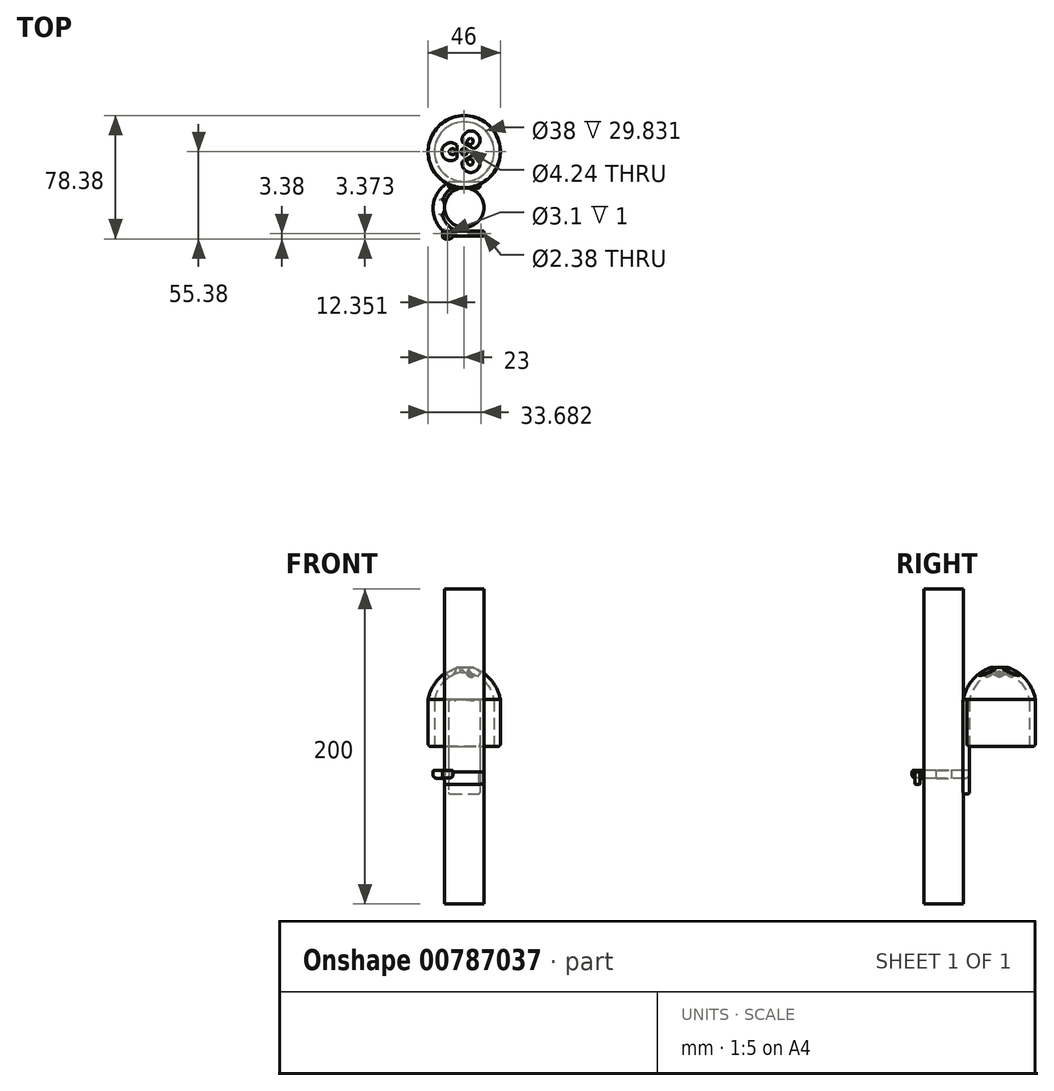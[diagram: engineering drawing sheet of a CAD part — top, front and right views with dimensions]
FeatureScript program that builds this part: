
annotation { "Feature Type Name" : "Feature", "Feature Type Description" : "" }
export const myFeature = defineFeature(function(context is Context, id is Id, definition is map)
    precondition{}
    {
        {
            var Q0;
            Q0=qCreatedBy(makeId("Top.planeOp"),FACE);
            var sketch = newSketch(context, id + "F0", { "sketchPlane" : qUnion([Q0])});
            skCircle(sketch, "E0", {"center": v(0, 0) * mm, "radius": 23 * mm});
            skSolve(sketch);
        }
        {
            var Q0;
            Q0 = qSketchRegion(id + "F0", true);
            extrude(context, id + "F1", {"entities" : qUnion([Q0]), "depth" : 30 * mm, "offsetDistance" : 25 * mm});
        }
        {
            var Q0;
            Q0=qCreatedBy(makeId("Top.planeOp"),FACE);
            var sketch = newSketch(context, id + "F2", { "sketchPlane" : qUnion([Q0])});
            skCircle(sketch, "E1", {"center": v(0, 0) * mm, "radius": 19 * mm});
            skSolve(sketch);
        }
        {
            var Q0;
            Q0 = qSketchRegion(id + "F2", true);
            extrude(context, id + "F3", {"entities" : qUnion([Q0]), "operationType" : NewBodyOperationType.REMOVE, "depth" : 30 * mm, "offsetDistance" : 25 * mm});
        }
        {
            var Q0;
            Q0=qCreatedBy(makeId("Front.planeOp"),FACE);
            cPlane(context, id + "F4", {"entities" : qUnion([Q0]), "cplaneType" : CPlaneType.OFFSET, "offset" : 21 * mm, "width" : 150 * mm, "height" : 150 * mm});
        }
        {
            var Q0;
            Q0=qCreatedBy(id+"F4.planeOp",FACE);
            var sketch = newSketch(context, id + "F5", { "sketchPlane" : qUnion([Q0])});
            skLineSegment(sketch, "E2.bottom", {"start": v(-10, 30) * mm, "end": v(10, 30) * mm});
            skLineSegment(sketch, "E2.top", {"start": v(-10, -30) * mm, "end": v(10, -30) * mm});
            skLineSegment(sketch, "E2.left", {"start": v(-10, 30) * mm, "end": v(-10, -30) * mm});
            skLineSegment(sketch, "E2.right", {"start": v(10, 30) * mm, "end": v(10, -30) * mm});
            skPoint(sketch, "E2.middle", {"position": v(0, 0) * mm});
            skSolve(sketch);
        }
        {
            var Q0;
            Q0 = qSketchRegion(id + "F5", true);
            extrude(context, id + "F6", {"entities" : qUnion([Q0]), "operationType" : NewBodyOperationType.ADD, "endBound" : BoundingType.SYMMETRIC, "depth" : 4 * mm, "offsetDistance" : 25 * mm});
        }
        {
            var Q0;
            Q0=qCreatedBy(makeId("Right.planeOp"),FACE);
            var sketch = newSketch(context, id + "F7", { "sketchPlane" : qUnion([Q0])});
            skArc(sketch, "E3", {"start": v(22.91, 29.83) * mm, "mid": v(15.03, 44.46) * mm, "end": v(0, 51.56) * mm});
            skLineSegment(sketch, "E4", {"start": v(22.91, 29.83) * mm, "end": v(18.91, 29.83) * mm});
            skLineSegment(sketch, "E5", {"start": v(0, 51.56) * mm, "end": v(0, 47.56) * mm});
            skArc(sketch, "E6", {"start": v(18.91, 29.83) * mm, "mid": v(12.4, 41.83) * mm, "end": v(0, 47.56) * mm});
            skSolve(sketch);
        }
        {
            var Q0;
            Q0=makeQuery(id+"F7.imprint","IMPRINT",FACE,{"disambiguationData":[TD([[makeQuery(id+"F7.imprint","IMPRINT",EDGE,{"derivedFrom":sQuery(id+"F7.wireOp",EDGE,"E3")}),1.0]])]});
            var Q1;
            Q1=sQuery(id+"F7.wireOp",EDGE,"E5");
            revolve(context, id + "F8", {"operationType" : NewBodyOperationType.ADD, "surfaceOperationType" : NewSurfaceOperationType.NEW, "entities" : qUnion([Q0]), "axis" : qUnion([Q1]), "revolveType" : RevolveType.FULL});
        }
        {
            var Q0;
            Q0=qCreatedBy(makeId("Top.planeOp"),FACE);
            var sketch = newSketch(context, id + "F9", { "sketchPlane" : qUnion([Q0])});
            skCircle(sketch, "E7", {"center": v(-7.43, 0) * mm, "radius": 1.87 * mm});
            skCircle(sketch, "E8.1.0", {"center": v(3.71, 6.43) * mm, "radius": 1.87 * mm});
            skCircle(sketch, "E8.2.0", {"center": v(3.71, -6.43) * mm, "radius": 1.87 * mm});
            skPoint(sketch, "E8.center", {"position": v(0, 0) * mm});
            skLineSegment(sketch, "E8.anchor1", {"start": v(0, 0) * mm, "end": v(-7.43, 0) * mm, "construction": true});
            skLineSegment(sketch, "E8.anchor2", {"start": v(0, 0) * mm, "end": v(3.71, -6.43) * mm, "construction": true});
            skCircle(sketch, "E9", {"center": v(0, 0) * mm, "radius": 2.12 * mm});
            skSolve(sketch);
        }
        {
            var Q0;
            Q0=makeQuery(id+"F9.imprint","IMPRINT",FACE,{"disambiguationData":[TD([[makeQuery(id+"F9.imprint","IMPRINT",EDGE,{"derivedFrom":sQuery(id+"F9.wireOp",EDGE,"E9")}),1.0]])]});
            var Q1;
            Q1=makeQuery(id+"F9.imprint","IMPRINT",FACE,{"disambiguationData":[TD([[makeQuery(id+"F9.imprint","IMPRINT",EDGE,{"derivedFrom":sQuery(id+"F9.wireOp",EDGE,"E7")}),1.0]])]});
            var Q2;
            Q2=makeQuery(id+"F9.imprint","IMPRINT",FACE,{"disambiguationData":[TD([[makeQuery(id+"F9.imprint","IMPRINT",EDGE,{"derivedFrom":sQuery(id+"F9.wireOp",EDGE,"E8.1.0")}),1.0]])]});
            var Q3;
            Q3=makeQuery(id+"F9.imprint","IMPRINT",FACE,{"disambiguationData":[TD([[makeQuery(id+"F9.imprint","IMPRINT",EDGE,{"derivedFrom":sQuery(id+"F9.wireOp",EDGE,"E8.2.0")}),1.0]])]});
            extrude(context, id + "F10", {"entities" : qUnion([Q0, Q1, Q2, Q3]), "operationType" : NewBodyOperationType.REMOVE, "endBound" : BoundingType.THROUGH_ALL, "depth" : 25 * mm, "offsetDistance" : 25 * mm});
        }
        {
            var Q0;
            Q0=qCreatedBy(makeId("Front.planeOp"),FACE);
            var sketch = newSketch(context, id + "F11", { "sketchPlane" : qUnion([Q0])});
            skPoint(sketch, "E10", {"position": v(-4.85, -20.06) * mm});
            skSolve(sketch);
        }
        {
            var Q0;
            Q0=sQuery(id+"F11.wireOp",VERTEX,"E10");
            var Q1;
            Q1=qCreatedBy(makeId("Top.planeOp"),FACE);
            cPlane(context, id + "F12", {"entities" : qUnion([Q0, Q1]), "cplaneType" : CPlaneType.PLANE_POINT, "offset" : 25 * mm, "width" : 150 * mm, "height" : 150 * mm});
        }
        {
            var Q0;
            Q0=qCreatedBy(id+"F12.planeOp",FACE);
            var sketch = newSketch(context, id + "F13", { "sketchPlane" : qUnion([Q0])});
            skPoint(sketch, "E11.second.point", {"position": v(-3.53, -23.55) * mm});
            skArc(sketch, "E12", {"start": v(-7.93, -23) * mm, "mid": v(-14.65, -36.3) * mm, "end": v(-7.21, -49.21) * mm});
            skArc(sketch, "E13", {"start": v(-9.46, -19.23) * mm, "mid": v(-19.78, -36.18) * mm, "end": v(-9.46, -53.12) * mm});
            skLineSegment(sketch, "E14", {"start": v(-7.93, -23) * mm, "end": v(-9.46, -19.23) * mm});
            skArc(sketch, "E15.MirrorCS", {"start": v(9.46, -19.23) * mm, "mid": v(19.78, -36.18) * mm, "end": v(9.46, -53.12) * mm});
            skLineSegment(sketch, "E16.MirrorCS", {"start": v(7.93, -23) * mm, "end": v(9.46, -19.23) * mm});
            skArc(sketch, "E17.MirrorCS", {"start": v(7.93, -23) * mm, "mid": v(14.65, -36.3) * mm, "end": v(7.21, -49.21) * mm});
            skLineSegment(sketch, "E18.top", {"start": v(-9.21, -55.38) * mm, "end": v(-11.96, -55.38) * mm});
            skLineSegment(sketch, "E18.left", {"start": v(-7.21, -49.21) * mm, "end": v(-7.21, -53.38) * mm});
            skLineSegment(sketch, "E18.right", {"start": v(-13.96, -49.74) * mm, "end": v(-13.96, -53.38) * mm});
            skLineSegment(sketch, "E19.MirrorCS", {"start": v(7.21, -49.21) * mm, "end": v(7.21, -53.38) * mm});
            skLineSegment(sketch, "E20.MirrorCS", {"start": v(9.21, -55.38) * mm, "end": v(11.96, -55.38) * mm});
            skLineSegment(sketch, "E21.MirrorCS", {"start": v(13.96, -49.74) * mm, "end": v(13.96, -53.38) * mm});
            skPoint(sketch, "E22.visualSharp", {"position": v(13.96, -55.38) * mm});
            skArc(sketch, "E22.filletArc", {"start": v(11.96, -55.38) * mm, "mid": v(13.37, -54.8) * mm, "end": v(13.96, -53.38) * mm});
            skPoint(sketch, "E23.visualSharp", {"position": v(7.21, -55.38) * mm});
            skArc(sketch, "E23.filletArc", {"start": v(7.21, -53.38) * mm, "mid": v(7.8, -54.8) * mm, "end": v(9.21, -55.38) * mm});
            skPoint(sketch, "E24.visualSharp", {"position": v(-7.21, -55.38) * mm});
            skArc(sketch, "E24.filletArc", {"start": v(-9.21, -55.38) * mm, "mid": v(-7.8, -54.8) * mm, "end": v(-7.21, -53.38) * mm});
            skPoint(sketch, "E25.visualSharp", {"position": v(-13.96, -55.38) * mm});
            skArc(sketch, "E25.filletArc", {"start": v(-13.96, -53.38) * mm, "mid": v(-13.37, -54.8) * mm, "end": v(-11.96, -55.38) * mm});
            skPoint(sketch, "E26", {"position": v(-11.02, -52.23) * mm});
            skPoint(sketch, "E27.MirrorP", {"position": v(11.02, -52.23) * mm});
            skArc(sketch, "E28", {"start": v(-14.02, -40.31) * mm, "mid": v(-12.35, -35.41) * mm, "end": v(-13.68, -30.4) * mm});
            skArc(sketch, "E29.MirrorCS", {"start": v(14.02, -40.31) * mm, "mid": v(12.35, -35.41) * mm, "end": v(13.68, -30.4) * mm});
            skSolve(sketch);
        }
        {
            var Q0;
            Q0=makeQuery(id+"F13.imprint","IMPRINT",FACE,{"disambiguationData":[TD([[makeQuery(id+"F13.imprint","IMPRINT",EDGE,{"derivedFrom":sQuery(id+"F13.wireOp",EDGE,"E12")}),-1.0]])]});
            var Q1;
            Q1=makeQuery(id+"F13.imprint","IMPRINT",FACE,{"disambiguationData":[TD([[makeQuery(id+"F13.imprint","IMPRINT",EDGE,{"derivedFrom":sQuery(id+"F13.wireOp",EDGE,"E15.MirrorCS")}),-1.0]])]});
            var Q2;
            {var subQ0=sQuery(id+"F13.wireOp",EDGE,"E28");Q2=makeQuery(id+"F13.imprint","IMPRINT",FACE,{"disambiguationData":[TD([[makeQuery(id+"F13.imprint","IMPRINT",EDGE,{"derivedFrom":subQ0}),1.0]])]});}
            var Q3;
            {var subQ0=sQuery(id+"F13.wireOp",EDGE,"E29.MirrorCS");Q3=makeQuery(id+"F13.imprint","IMPRINT",FACE,{"disambiguationData":[TD([[makeQuery(id+"F13.imprint","IMPRINT",EDGE,{"derivedFrom":subQ0}),-1.0]])]});}
            extrude(context, id + "F14", {"entities" : qUnion([Q0, Q1, Q2, Q3]), "operationType" : NewBodyOperationType.ADD, "depth" : 5 * mm, "offsetDistance" : 25 * mm});
        }
        {
            var Q0;
            Q0=makeQuery(id+"F3.boolean.opBoolean","COPY",EDGE,{"derivedFrom":makeQuery(id+"F3.opExtrude","CAP_EDGE",EDGE,{"disambiguationData":[OSD([sQuery(id+"F2.wireOp",EDGE,"E1")])],"isStart":true})});
            var Q1;
            {var subQ0=sQuery(id+"F0.wireOp",EDGE,"E0");Q1=makeQuery(id+"F6.boolean.opBoolean","SPLIT",EDGE,{"disambiguationData":[TD([makeQuery(id+"F6.opExtrude","SWEPT_FACE",FACE,{"disambiguationData":[OSD([sQuery(id+"F5.wireOp",EDGE,"E2.left")])]})])],"derivedFrom":makeQuery(id+"F1.opExtrude","CAP_EDGE",EDGE,{"disambiguationData":[OSD([subQ0])],"isStart":true})});}
            fillet(context, id + "F15", {"entities" : qUnion([Q0, Q1]), "radius" : 2 * mm, "tangentPropagation" : true, "allowEdgeOverflow" : false});
        }
        {
            var Q0;
            Q0=qCreatedBy(makeId("Top.planeOp"),FACE);
            var sketch = newSketch(context, id + "F16", { "sketchPlane" : qUnion([Q0])});
            skCircle(sketch, "E30", {"center": v(0, -35.47) * mm, "radius": 12.5 * mm});
            skSolve(sketch);
        }
        {
            var Q0;
            Q0 = qSketchRegion(id + "F16", true);
            extrude(context, id + "F17", {"entities" : qUnion([Q0]), "endBound" : BoundingType.SYMMETRIC, "depth" : 200 * mm, "offsetDistance" : 25 * mm});
        }
        {
            var Q0;
            Q0=makeQuery(id+"F14.opExtrude","CAP_FACE",FACE,{"disambiguationData":[OSD([sQuery(id+"F13.wireOp",EDGE,"E12"),sQuery(id+"F13.wireOp",EDGE,"E13"),sQuery(id+"F13.wireOp",EDGE,"E14"),sQuery(id+"F13.wireOp",EDGE,"E18.top"),sQuery(id+"F13.wireOp",EDGE,"E18.left"),sQuery(id+"F13.wireOp",EDGE,"E18.right"),sQuery(id+"F13.wireOp",EDGE,"E24.filletArc"),sQuery(id+"F13.wireOp",EDGE,"E25.filletArc")])],"isStart":true});
            var sketch = newSketch(context, id + "F18", { "sketchPlane" : qUnion([Q0])});
            skCircle(sketch, "E31", {"center": v(-10.65, 52) * mm, "radius": 1.55 * mm});
            skCircle(sketch, "E32.MirrorC", {"center": v(10.65, 52) * mm, "radius": 1.55 * mm});
            skSolve(sketch);
        }
        {
            var Q0;
            Q0=makeQuery(id+"F18.imprint","IMPRINT",FACE,{"disambiguationData":[TD([[makeQuery(id+"F18.imprint","IMPRINT",EDGE,{"derivedFrom":sQuery(id+"F18.wireOp",EDGE,"E31")}),1.0]])]});
            var Q1;
            Q1=makeQuery(id+"F18.imprint","IMPRINT",FACE,{"disambiguationData":[TD([[makeQuery(id+"F18.imprint","IMPRINT",EDGE,{"derivedFrom":sQuery(id+"F18.wireOp",EDGE,"E32.MirrorC")}),-1.0]])]});
            extrude(context, id + "F19", {"entities" : qUnion([Q0, Q1]), "operationType" : NewBodyOperationType.REMOVE, "endBound" : BoundingType.THROUGH_ALL, "oppositeDirection" : true, "depth" : 25 * mm, "offsetDistance" : 25 * mm});
        }
        {
            var Q0;
            Q0=makeQuery(id+"F10.boolean.opBoolean","INTERSECT",EDGE,{"derivedFrom":[makeQuery(id+"F8.opRevolve","SWEPT_FACE",FACE,{"disambiguationData":[OSD([sQuery(id+"F7.wireOp",EDGE,"E3")])]}),makeQuery(id+"F10.opExtrude","SWEPT_FACE",FACE,{"disambiguationData":[OSD([sQuery(id+"F9.wireOp",EDGE,"E9")])]})]});
            var Q1;
            Q1=makeQuery(id+"F10.boolean.opBoolean","INTERSECT",EDGE,{"derivedFrom":[makeQuery(id+"F8.opRevolve","SWEPT_FACE",FACE,{"disambiguationData":[OSD([sQuery(id+"F7.wireOp",EDGE,"E3")])]}),makeQuery(id+"F10.opExtrude","SWEPT_FACE",FACE,{"disambiguationData":[OSD([sQuery(id+"F9.wireOp",EDGE,"E8.2.0")])]})]});
            var Q2;
            Q2=makeQuery(id+"F10.boolean.opBoolean","INTERSECT",EDGE,{"derivedFrom":[makeQuery(id+"F8.opRevolve","SWEPT_FACE",FACE,{"disambiguationData":[OSD([sQuery(id+"F7.wireOp",EDGE,"E3")])]}),makeQuery(id+"F10.opExtrude","SWEPT_FACE",FACE,{"disambiguationData":[OSD([sQuery(id+"F9.wireOp",EDGE,"E8.1.0")])]})]});
            var Q3;
            Q3=makeQuery(id+"F10.boolean.opBoolean","INTERSECT",EDGE,{"derivedFrom":[makeQuery(id+"F8.opRevolve","SWEPT_FACE",FACE,{"disambiguationData":[OSD([sQuery(id+"F7.wireOp",EDGE,"E3")])]}),makeQuery(id+"F10.opExtrude","SWEPT_FACE",FACE,{"disambiguationData":[OSD([sQuery(id+"F9.wireOp",EDGE,"E7")])]})]});
            fillet(context, id + "F20", {"entities" : qUnion([Q0, Q1, Q2, Q3]), "radius" : 3 * mm, "tangentPropagation" : true, "allowEdgeOverflow" : false});
        }
        {
            var Q0;
            {var subQ0=sQuery(id+"F13.wireOp",EDGE,"E15.MirrorCS");Q0=makeQuery(id+"F14.boolean.opBoolean","SPLIT",EDGE,{"disambiguationData":[TD([makeQuery(id+"F6.opExtrude","SWEPT_FACE",FACE,{"disambiguationData":[OSD([sQuery(id+"F5.wireOp",EDGE,"E2.right")])]})])],"derivedFrom":makeQuery(id+"F14.opExtrude","CAP_EDGE",EDGE,{"disambiguationData":[OSD([subQ0])],"isStart":true})});}
            var Q1;
            {var subQ0=sQuery(id+"F13.wireOp",EDGE,"E17.MirrorCS");Q1=makeQuery(id+"F14.opExtrude","CAP_EDGE",EDGE,{"disambiguationData":[OSD([subQ0]),TDD([makeQuery(id+"F13.imprint","IMPRINT",EDGE,{"disambiguationData":[TD([[makeQuery(id+"F13.imprint","INTERSECT",VERTEX,{"derivedFrom":[subQ0,sQuery(id+"F13.wireOp",EDGE,"E19.MirrorCS")]}),1.0]])],"derivedFrom":subQ0})])],"isStart":true});}
            var Q2;
            Q2=makeQuery(id+"F14.opExtrude","CAP_EDGE",EDGE,{"disambiguationData":[OSD([sQuery(id+"F13.wireOp",EDGE,"E29.MirrorCS")])],"isStart":true});
            var Q3;
            {var subQ0=sQuery(id+"F13.wireOp",EDGE,"E17.MirrorCS");Q3=makeQuery(id+"F14.opExtrude","CAP_EDGE",EDGE,{"disambiguationData":[OSD([subQ0]),TDD([makeQuery(id+"F13.imprint","IMPRINT",EDGE,{"disambiguationData":[TD([[makeQuery(id+"F13.imprint","INTERSECT",VERTEX,{"derivedFrom":[sQuery(id+"F13.wireOp",EDGE,"E16.MirrorCS"),subQ0]}),-1.0]])],"derivedFrom":subQ0})])],"isStart":true});}
            var Q4;
            Q4=makeQuery(id+"F14.opExtrude","CAP_EDGE",EDGE,{"disambiguationData":[OSD([sQuery(id+"F13.wireOp",EDGE,"E19.MirrorCS")])],"isStart":true});
            var Q5;
            Q5=makeQuery(id+"F14.opExtrude","CAP_EDGE",EDGE,{"disambiguationData":[OSD([sQuery(id+"F13.wireOp",EDGE,"E18.left")])],"isStart":true});
            var Q6;
            {var subQ1=sQuery(id+"F13.wireOp",EDGE,"E13");Q6=makeQuery(id+"F14.boolean.opBoolean","SPLIT",EDGE,{"disambiguationData":[TD([makeQuery(id+"F6.opExtrude","SWEPT_FACE",FACE,{"disambiguationData":[OSD([sQuery(id+"F5.wireOp",EDGE,"E2.left")])]})])],"derivedFrom":makeQuery(id+"F14.opExtrude","CAP_EDGE",EDGE,{"disambiguationData":[OSD([subQ1])],"isStart":true})});}
            var Q7;
            {var subQ0=sQuery(id+"F13.wireOp",EDGE,"E12");Q7=makeQuery(id+"F14.opExtrude","CAP_EDGE",EDGE,{"disambiguationData":[OSD([subQ0]),TDD([makeQuery(id+"F13.imprint","IMPRINT",EDGE,{"disambiguationData":[TD([[makeQuery(id+"F13.imprint","INTERSECT",VERTEX,{"derivedFrom":[subQ0,sQuery(id+"F13.wireOp",EDGE,"E18.left")]}),1.0]])],"derivedFrom":subQ0})])],"isStart":true});}
            var Q8;
            Q8=makeQuery(id+"F14.opExtrude","CAP_EDGE",EDGE,{"disambiguationData":[OSD([sQuery(id+"F13.wireOp",EDGE,"E28")])],"isStart":true});
            var Q9;
            {var subQ0=sQuery(id+"F13.wireOp",EDGE,"E12");Q9=makeQuery(id+"F14.opExtrude","CAP_EDGE",EDGE,{"disambiguationData":[OSD([subQ0]),TDD([makeQuery(id+"F13.imprint","IMPRINT",EDGE,{"disambiguationData":[TD([[makeQuery(id+"F13.imprint","INTERSECT",VERTEX,{"derivedFrom":[subQ0,sQuery(id+"F13.wireOp",EDGE,"E14")]}),-1.0]])],"derivedFrom":subQ0})])],"isStart":true});}
            fillet(context, id + "F21", {"entities" : qUnion([Q0, Q1, Q2, Q3, Q4, Q5, Q6, Q7, Q8, Q9]), "radius" : 2 * mm, "tangentPropagation" : true, "allowEdgeOverflow" : false});
        }
        {
            var Q0;
            Q0=makeQuery(id+"F6.opExtrude","CAP_EDGE",EDGE,{"disambiguationData":[OSD([sQuery(id+"F5.wireOp",EDGE,"E2.top")])],"isStart":true});
            var Q1;
            Q1=makeQuery(id+"F15.opFillet","BLEND_EDGE",EDGE,{"blendedFrom":[makeQuery(id+"F3.boolean.opBoolean","COPY",EDGE,{"derivedFrom":makeQuery(id+"F3.opExtrude","CAP_EDGE",EDGE,{"disambiguationData":[OSD([sQuery(id+"F2.wireOp",EDGE,"E1")])],"isStart":true})}),makeQuery(id+"F6.opExtrude","CAP_FACE",FACE,{"disambiguationData":[OSD([sQuery(id+"F5.wireOp",EDGE,"E2.bottom"),sQuery(id+"F5.wireOp",EDGE,"E2.top"),sQuery(id+"F5.wireOp",EDGE,"E2.left"),sQuery(id+"F5.wireOp",EDGE,"E2.right")])],"isStart":true})],"blendedInto":[makeQuery(id+"F6.opExtrude","CAP_FACE",FACE,{"disambiguationData":[OSD([sQuery(id+"F5.wireOp",EDGE,"E2.bottom"),sQuery(id+"F5.wireOp",EDGE,"E2.top"),sQuery(id+"F5.wireOp",EDGE,"E2.left"),sQuery(id+"F5.wireOp",EDGE,"E2.right")])],"isStart":true})]});
            var Q2;
            Q2=makeQuery(id+"F6.opExtrude","CAP_EDGE",EDGE,{"disambiguationData":[OSD([sQuery(id+"F5.wireOp",EDGE,"E2.top")])],"isStart":false});
            var Q3;
            {var subQ0=sQuery(id+"F5.wireOp",EDGE,"E2.left");var subQ1=sQuery(id+"F5.wireOp",EDGE,"E2.top");Q3=makeQuery(id+"F14.boolean.opBoolean","SPLIT",EDGE,{"disambiguationData":[TD([makeQuery(id+"F6.opExtrude","SWEPT_FACE",FACE,{"disambiguationData":[OSD([subQ1])]})])],"derivedFrom":makeQuery(id+"F6.opExtrude","CAP_EDGE",EDGE,{"disambiguationData":[OSD([subQ0])],"isStart":false})});}
            var Q4;
            {var subQ0=sQuery(id+"F5.wireOp",EDGE,"E2.right");var subQ1=sQuery(id+"F5.wireOp",EDGE,"E2.top");Q4=makeQuery(id+"F14.boolean.opBoolean","SPLIT",EDGE,{"disambiguationData":[TD([makeQuery(id+"F6.opExtrude","SWEPT_FACE",FACE,{"disambiguationData":[OSD([subQ1])]})])],"derivedFrom":makeQuery(id+"F6.opExtrude","CAP_EDGE",EDGE,{"disambiguationData":[OSD([subQ0])],"isStart":false})});}
            var Q5;
            {var subQ0=sQuery(id+"F5.wireOp",EDGE,"E2.right");Q5=makeQuery(id+"F14.boolean.opBoolean","SPLIT",EDGE,{"disambiguationData":[TD([makeQuery(id+"F1.opExtrude","CAP_FACE",FACE,{"disambiguationData":[OSD([sQuery(id+"F0.wireOp",EDGE,"E0")])],"isStart":false})])],"derivedFrom":makeQuery(id+"F6.opExtrude","CAP_EDGE",EDGE,{"disambiguationData":[OSD([subQ0])],"isStart":false})});}
            var Q6;
            {var subQ0=sQuery(id+"F5.wireOp",EDGE,"E2.left");Q6=makeQuery(id+"F14.boolean.opBoolean","SPLIT",EDGE,{"disambiguationData":[TD([makeQuery(id+"F1.opExtrude","CAP_FACE",FACE,{"disambiguationData":[OSD([sQuery(id+"F0.wireOp",EDGE,"E0")])],"isStart":false})])],"derivedFrom":makeQuery(id+"F6.opExtrude","CAP_EDGE",EDGE,{"disambiguationData":[OSD([subQ0])],"isStart":false})});}
            var Q7;
            {var subQ0=sQuery(id+"F5.wireOp",EDGE,"E2.bottom");var subQ2=sQuery(id+"F5.wireOp",EDGE,"E2.left");Q7=makeQuery(id+"F6.boolean.opBoolean","SPLIT",EDGE,{"disambiguationData":[TD([makeQuery(id+"F6.opExtrude","SWEPT_FACE",FACE,{"disambiguationData":[OSD([subQ2])]})])],"derivedFrom":makeQuery(id+"F6.opExtrude","CAP_EDGE",EDGE,{"disambiguationData":[OSD([subQ0])],"isStart":false})});}
            var Q8;
            {var subQ0=sQuery(id+"F5.wireOp",EDGE,"E2.bottom");var subQ2=sQuery(id+"F5.wireOp",EDGE,"E2.right");Q8=makeQuery(id+"F6.boolean.opBoolean","SPLIT",EDGE,{"disambiguationData":[TD([makeQuery(id+"F6.opExtrude","SWEPT_FACE",FACE,{"disambiguationData":[OSD([subQ2])]})])],"derivedFrom":makeQuery(id+"F6.opExtrude","CAP_EDGE",EDGE,{"disambiguationData":[OSD([subQ0])],"isStart":false})});}
            var Q9;
            Q9=makeQuery(id+"F6.opExtrude","CAP_EDGE",EDGE,{"disambiguationData":[OSD([sQuery(id+"F5.wireOp",EDGE,"E2.left")])],"isStart":true});
            var Q10;
            Q10=makeQuery(id+"F6.opExtrude","CAP_EDGE",EDGE,{"disambiguationData":[OSD([sQuery(id+"F5.wireOp",EDGE,"E2.right")])],"isStart":true});
            var Q11;
            Q11=makeQuery(id+"F6.opExtrude","SWEPT_EDGE",EDGE,{"disambiguationData":[OSD([sQuery(id+"F5.wireOp",EDGE,"E2.top"),sQuery(id+"F5.wireOp",EDGE,"E2.left")])]});
            var Q12;
            Q12=makeQuery(id+"F6.opExtrude","SWEPT_EDGE",EDGE,{"disambiguationData":[OSD([sQuery(id+"F5.wireOp",EDGE,"E2.top"),sQuery(id+"F5.wireOp",EDGE,"E2.right")])]});
            fillet(context, id + "F22", {"entities" : qUnion([Q0, Q1, Q2, Q3, Q4, Q5, Q6, Q7, Q8, Q9, Q10, Q11, Q12]), "radius" : 1 * mm, "tangentPropagation" : true, "allowEdgeOverflow" : false});
        }
        {
            var Q0;
            Q0=makeQuery(id+"F14.opExtrude","CAP_EDGE",EDGE,{"disambiguationData":[OSD([sQuery(id+"F13.wireOp",EDGE,"E29.MirrorCS")])],"isStart":false});
            var Q1;
            {var subQ0=sQuery(id+"F13.wireOp",EDGE,"E17.MirrorCS");Q1=makeQuery(id+"F14.opExtrude","CAP_EDGE",EDGE,{"disambiguationData":[OSD([subQ0]),TDD([makeQuery(id+"F13.imprint","IMPRINT",EDGE,{"disambiguationData":[TD([[makeQuery(id+"F13.imprint","INTERSECT",VERTEX,{"derivedFrom":[sQuery(id+"F13.wireOp",EDGE,"E16.MirrorCS"),subQ0]}),-1.0]])],"derivedFrom":subQ0})])],"isStart":false});}
            var Q2;
            {var subQ0=sQuery(id+"F13.wireOp",EDGE,"E17.MirrorCS");Q2=makeQuery(id+"F14.opExtrude","CAP_EDGE",EDGE,{"disambiguationData":[OSD([subQ0]),TDD([makeQuery(id+"F13.imprint","IMPRINT",EDGE,{"disambiguationData":[TD([[makeQuery(id+"F13.imprint","INTERSECT",VERTEX,{"derivedFrom":[subQ0,sQuery(id+"F13.wireOp",EDGE,"E19.MirrorCS")]}),1.0]])],"derivedFrom":subQ0})])],"isStart":false});}
            var Q3;
            Q3=makeQuery(id+"F14.opExtrude","CAP_EDGE",EDGE,{"disambiguationData":[OSD([sQuery(id+"F13.wireOp",EDGE,"E19.MirrorCS")])],"isStart":false});
            var Q4;
            Q4=makeQuery(id+"F14.opExtrude","CAP_EDGE",EDGE,{"disambiguationData":[OSD([sQuery(id+"F13.wireOp",EDGE,"E21.MirrorCS")])],"isStart":false});
            var Q5;
            {var subQ0=sQuery(id+"F13.wireOp",EDGE,"E12");Q5=makeQuery(id+"F14.opExtrude","CAP_EDGE",EDGE,{"disambiguationData":[OSD([subQ0]),TDD([makeQuery(id+"F13.imprint","IMPRINT",EDGE,{"disambiguationData":[TD([[makeQuery(id+"F13.imprint","INTERSECT",VERTEX,{"derivedFrom":[subQ0,sQuery(id+"F13.wireOp",EDGE,"E14")]}),-1.0]])],"derivedFrom":subQ0})])],"isStart":false});}
            var Q6;
            Q6=makeQuery(id+"F14.opExtrude","CAP_EDGE",EDGE,{"disambiguationData":[OSD([sQuery(id+"F13.wireOp",EDGE,"E28")])],"isStart":false});
            var Q7;
            {var subQ0=sQuery(id+"F13.wireOp",EDGE,"E12");Q7=makeQuery(id+"F14.opExtrude","CAP_EDGE",EDGE,{"disambiguationData":[OSD([subQ0]),TDD([makeQuery(id+"F13.imprint","IMPRINT",EDGE,{"disambiguationData":[TD([[makeQuery(id+"F13.imprint","INTERSECT",VERTEX,{"derivedFrom":[subQ0,sQuery(id+"F13.wireOp",EDGE,"E18.left")]}),1.0]])],"derivedFrom":subQ0})])],"isStart":false});}
            var Q8;
            Q8=makeQuery(id+"F14.opExtrude","CAP_EDGE",EDGE,{"disambiguationData":[OSD([sQuery(id+"F13.wireOp",EDGE,"E18.left")])],"isStart":false});
            var Q9;
            Q9=makeQuery(id+"F14.opExtrude","CAP_EDGE",EDGE,{"disambiguationData":[OSD([sQuery(id+"F13.wireOp",EDGE,"E13")])],"isStart":false});
            var Q10;
            {var subQ0=sQuery(id+"F13.wireOp",EDGE,"E13");Q10=makeQuery(id+"F21.opFillet","BLEND_EDGE",EDGE,{"blendedFrom":[makeQuery(id+"F14.boolean.opBoolean","INTERSECT",EDGE,{"derivedFrom":[makeQuery(id+"F6.opExtrude","SWEPT_FACE",FACE,{"disambiguationData":[OSD([sQuery(id+"F5.wireOp",EDGE,"E2.left")])]}),makeQuery(id+"F14.opExtrude","CAP_FACE",FACE,{"disambiguationData":[OSD([sQuery(id+"F13.wireOp",EDGE,"E12"),subQ0,sQuery(id+"F13.wireOp",EDGE,"E14"),sQuery(id+"F13.wireOp",EDGE,"E18.top"),sQuery(id+"F13.wireOp",EDGE,"E18.left"),sQuery(id+"F13.wireOp",EDGE,"E18.right"),sQuery(id+"F13.wireOp",EDGE,"E24.filletArc"),sQuery(id+"F13.wireOp",EDGE,"E25.filletArc"),sQuery(id+"F13.wireOp",EDGE,"E28")])],"isStart":false})]}),makeQuery(id+"F14.opExtrude","SWEPT_FACE",FACE,{"disambiguationData":[OSD([subQ0])]})],"blendedInto":[makeQuery(id+"F14.opExtrude","SWEPT_FACE",FACE,{"disambiguationData":[OSD([subQ0])]})]});}
            var Q11;
            Q11=makeQuery(id+"F14.opExtrude","CAP_EDGE",EDGE,{"disambiguationData":[OSD([sQuery(id+"F13.wireOp",EDGE,"E15.MirrorCS")])],"isStart":false});
            var Q12;
            Q12=makeQuery(id+"F1.opExtrude","CAP_EDGE",EDGE,{"disambiguationData":[OSD([sQuery(id+"F0.wireOp",EDGE,"E0")])],"isStart":false});
            fillet(context, id + "F23", {"entities" : qUnion([Q0, Q1, Q2, Q3, Q4, Q5, Q6, Q7, Q8, Q9, Q10, Q11, Q12]), "radius" : .8 * mm, "tangentPropagation" : true, "allowEdgeOverflow" : false});
        }
        {
            var Q0;
            Q0=qCreatedBy(id+"F12.planeOp",FACE);
            var sketch = newSketch(context, id + "F24", { "sketchPlane" : qUnion([Q0])});
            skCircle(sketch, "E33", {"center": v(-10.66, -52) * mm, "radius": 1.2 * mm});
            skCircle(sketch, "E34.MirrorC", {"center": v(10.68, -52) * mm, "radius": 1.2 * mm});
            skLineSegment(sketch, "E35.bottom", {"start": v(-12.52, -50.35) * mm, "end": v(12.54, -50.35) * mm});
            skLineSegment(sketch, "E35.top", {"start": v(-12.52, -53.65) * mm, "end": v(12.54, -53.65) * mm});
            skLineSegment(sketch, "E35.left", {"start": v(-12.52, -50.35) * mm, "end": v(-12.52, -53.65) * mm});
            skLineSegment(sketch, "E35.right", {"start": v(12.54, -50.35) * mm, "end": v(12.54, -53.65) * mm});
            skSolve(sketch);
        }
        {
            var Q0;
            Q0 = qSketchRegion(id + "F24", true);
            extrude(context, id + "F25", {"entities" : qUnion([Q0]), "oppositeDirection" : true, "depth" : 4 * mm, "offsetDistance" : 25 * mm});
        }
        {
            var Q0;
            Q0=makeQuery(id+"F24.imprint","IMPRINT",FACE,{"disambiguationData":[TD([[makeQuery(id+"F24.imprint","IMPRINT",EDGE,{"derivedFrom":sQuery(id+"F24.wireOp",EDGE,"E33")}),1.0]])]});
            var Q1;
            Q1=makeQuery(id+"F24.imprint","IMPRINT",FACE,{"disambiguationData":[TD([[makeQuery(id+"F24.imprint","IMPRINT",EDGE,{"derivedFrom":sQuery(id+"F24.wireOp",EDGE,"E34.MirrorC")}),-1.0]])]});
            extrude(context, id + "F26", {"entities" : qUnion([Q0, Q1]), "operationType" : NewBodyOperationType.ADD, "endBound" : BoundingType.SYMMETRIC, "depth" : 8 * mm, "offsetDistance" : 25 * mm});
        }
        {
            var Q0;
            {var subQ0=sQuery(id+"F24.wireOp",EDGE,"E34.MirrorC");var subQ1=sQuery(id+"F24.wireOp",EDGE,"E33");Q0=makeQuery(id+"F26.boolean.opBoolean","MERGE",FACE,{"derivedFrom":[makeQuery(id+"F25.opExtrude","CAP_FACE",FACE,{"disambiguationData":[OSD([subQ1,subQ0,sQuery(id+"F24.wireOp",EDGE,"E35.bottom"),sQuery(id+"F24.wireOp",EDGE,"E35.top"),sQuery(id+"F24.wireOp",EDGE,"E35.left"),sQuery(id+"F24.wireOp",EDGE,"E35.right")])],"isStart":false}),makeQuery(id+"F26.opExtrude","CAP_FACE",FACE,{"disambiguationData":[OSD([subQ1])],"isStart":true}),makeQuery(id+"F26.opExtrude","CAP_FACE",FACE,{"disambiguationData":[OSD([subQ0])],"isStart":true})]});}
            var Q1;
            Q1=makeQuery(id+"F25.opExtrude","SWEPT_EDGE",EDGE,{"disambiguationData":[OSD([sQuery(id+"F24.wireOp",EDGE,"E35.top"),sQuery(id+"F24.wireOp",EDGE,"E35.right")])]});
            var Q2;
            Q2=makeQuery(id+"F25.opExtrude","SWEPT_EDGE",EDGE,{"disambiguationData":[OSD([sQuery(id+"F24.wireOp",EDGE,"E35.bottom"),sQuery(id+"F24.wireOp",EDGE,"E35.right")])]});
            var Q3;
            Q3=makeQuery(id+"F25.opExtrude","SWEPT_EDGE",EDGE,{"disambiguationData":[OSD([sQuery(id+"F24.wireOp",EDGE,"E35.top"),sQuery(id+"F24.wireOp",EDGE,"E35.left")])]});
            var Q4;
            Q4=makeQuery(id+"F25.opExtrude","SWEPT_EDGE",EDGE,{"disambiguationData":[OSD([sQuery(id+"F24.wireOp",EDGE,"E35.bottom"),sQuery(id+"F24.wireOp",EDGE,"E35.left")])]});
            var Q5;
            Q5=makeQuery(id+"F25.opExtrude","CAP_EDGE",EDGE,{"disambiguationData":[OSD([sQuery(id+"F24.wireOp",EDGE,"E35.bottom")])],"isStart":true});
            var Q6;
            Q6=makeQuery(id+"F25.opExtrude","CAP_EDGE",EDGE,{"disambiguationData":[OSD([sQuery(id+"F24.wireOp",EDGE,"E35.top")])],"isStart":true});
            var Q7;
            Q7=makeQuery(id+"F26.opExtrude","CAP_EDGE",EDGE,{"disambiguationData":[OSD([sQuery(id+"F24.wireOp",EDGE,"E34.MirrorC")])],"isStart":false});
            var Q8;
            Q8=makeQuery(id+"F26.opExtrude","CAP_EDGE",EDGE,{"disambiguationData":[OSD([sQuery(id+"F24.wireOp",EDGE,"E33")])],"isStart":false});
            var Q9;
            Q9=makeQuery(id+"F25.opExtrude","CAP_EDGE",EDGE,{"disambiguationData":[OSD([sQuery(id+"F24.wireOp",EDGE,"E35.left")])],"isStart":true});
            fillet(context, id + "F27", {"entities" : qUnion([Q0, Q1, Q2, Q3, Q4, Q5, Q6, Q7, Q8, Q9]), "radius" : .8 * mm, "tangentPropagation" : true, "allowEdgeOverflow" : false});
        }
    });
